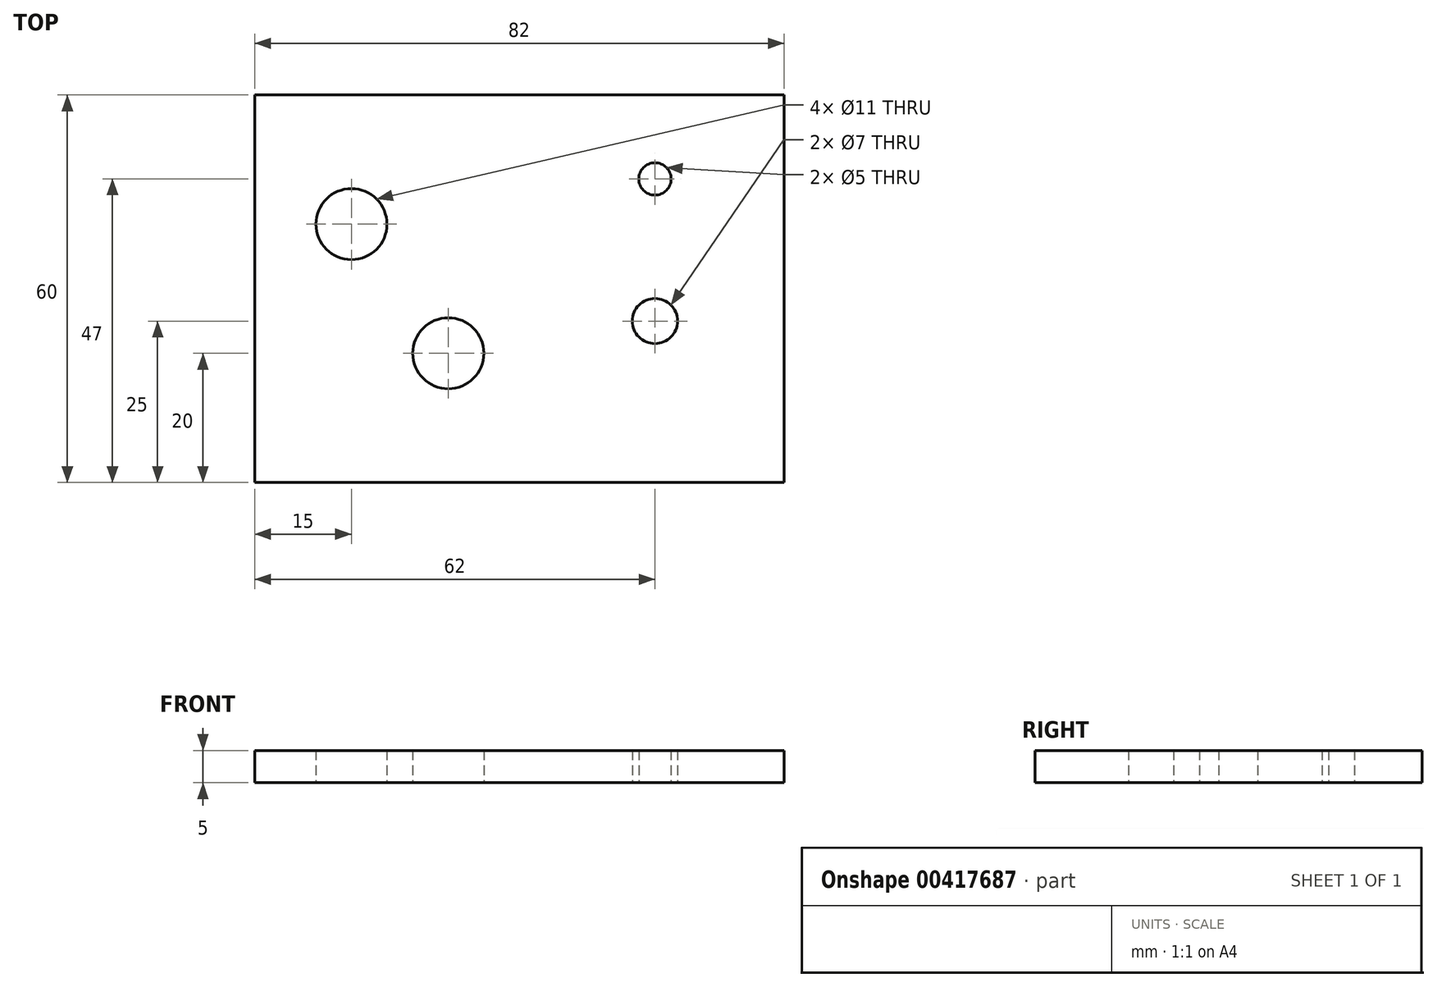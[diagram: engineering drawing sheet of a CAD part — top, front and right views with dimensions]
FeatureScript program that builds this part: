
annotation { "Feature Type Name" : "Feature", "Feature Type Description" : "" }
export const myFeature = defineFeature(function(context is Context, id is Id, definition is map)
    precondition{}
    {
        {
            var Q0;
            Q0=qCreatedBy(makeId("Top.planeOp"),FACE);
            var sketch = newSketch(context, id + "F0", { "sketchPlane" : qUnion([Q0])});
            skLineSegment(sketch, "E0.bottom", {"start": v(41, -30) * mm, "end": v(-41, -30) * mm});
            skLineSegment(sketch, "E0.top", {"start": v(41, 30) * mm, "end": v(-41, 30) * mm});
            skLineSegment(sketch, "E0.left", {"start": v(41, -30) * mm, "end": v(41, 30) * mm});
            skLineSegment(sketch, "E0.right", {"start": v(-41, -30) * mm, "end": v(-41, 30) * mm});
            skPoint(sketch, "E0.middle", {"position": v(0, 0) * mm});
            skCircle(sketch, "E1", {"center": v(21, -5) * mm, "radius": 3.5 * mm});
            skCircle(sketch, "E2", {"center": v(-26, 10) * mm, "radius": 5.5 * mm});
            skCircle(sketch, "E3", {"center": v(-11, -10) * mm, "radius": 5.5 * mm});
            skCircle(sketch, "E4", {"center": v(21, 17) * mm, "radius": 2.5 * mm});
            skCircle(sketch, "E5", {"center": v(-26, 10) * mm, "radius": 3 * mm});
            skCircle(sketch, "E6", {"center": v(-11, -10) * mm, "radius": 3 * mm});
            skSolve(sketch);
        }
        {
            var Q0;
            Q0=makeQuery(id+"F0.imprint","IMPRINT",FACE,{"disambiguationData":[TD([[makeQuery(id+"F0.imprint","IMPRINT",EDGE,{"derivedFrom":sQuery(id+"F0.wireOp",EDGE,"E0.bottom")}),-1.0]])]});
            var Q1;
            Q1=makeQuery(id+"F0.imprint","IMPRINT",FACE,{"disambiguationData":[TD([[makeQuery(id+"F0.imprint","IMPRINT",EDGE,{"derivedFrom":sQuery(id+"F0.wireOp",EDGE,"E3")}),-1.0]])]});
            var Q2;
            Q2=makeQuery(id+"F0.imprint","IMPRINT",FACE,{"disambiguationData":[TD([[makeQuery(id+"F0.imprint","IMPRINT",EDGE,{"derivedFrom":sQuery(id+"F0.wireOp",EDGE,"E2")}),-1.0]])]});
            extrude(context, id + "F1", {"entities" : qUnion([Q0, Q1, Q2]), "depth" : 5 * mm});
        }
    });
